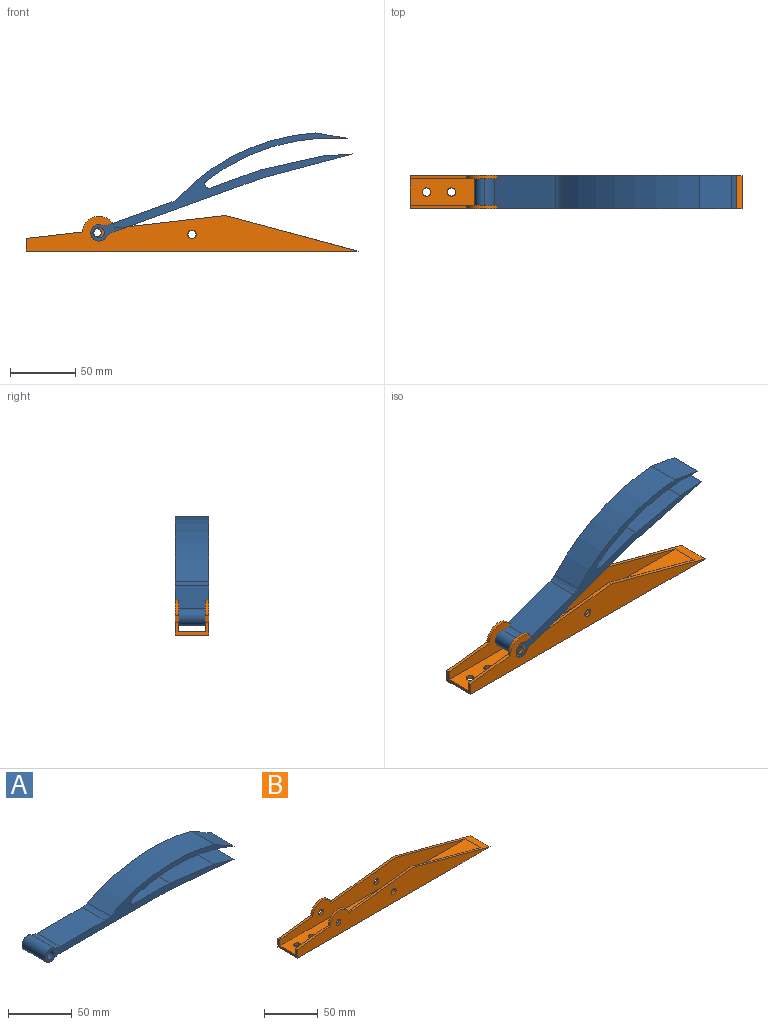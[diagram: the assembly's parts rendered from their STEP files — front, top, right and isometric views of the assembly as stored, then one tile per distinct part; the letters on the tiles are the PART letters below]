
ASSEMBLY  parts=2 mates=1
PART A: 17 faces, bbox 209.6x25.4x31.2 mm
  f0: plane 48.61x25.4mm, normal (0.13,0,0.99), area 1245.1mm2, adj f1,f9,f11,f12
  f1: plane 40.6x25.4mm, normal (0,0,1), area 1031.2mm2, adj f0,f11,f12,f16
  f2: cylinder r=157.48mm len=112.42mm, axis (0,-1,0), area 2924.4mm2, adj f3,f11,f12,f16
  f3: plane 25.4x21.43mm, normal (0.49,0,0.87), area 626mm2, adj f2,f4,f11,f12
  f4: cylinder r=157.48mm len=115.62mm, axis (0,-1,0), area 3020.8mm2, adj f3,f11,f12,f13
  f5: plane 49.86x25.4mm, normal (0,0,1), area 1266.5mm2, adj f11,f12,f13,f14
  f6: cylinder r=6.35mm len=25.4mm, axis (0,-1,0), area 695.6mm2, adj f11,f12,f14,f15
  f7: plane 121.82x25.4mm, normal (0,0,-1), area 3094.3mm2, adj f8,f11,f12,f15
  f8: plane 70.85x25.4mm, normal (-0.09,0,-1), area 1806.7mm2, adj f7,f9,f11,f12
  f9: plane 25.4x22.24mm, normal (0.27,0,0.96), area 587.5mm2, adj f0,f8,f11,f12
  f10: cylinder r=3.94mm len=25.4mm, axis (0,-1,0), area 628.3mm2, adj f11,f12
  f11: plane 209.55x31.21mm, normal (0,1,0), area 1830.8mm2, adj f0,f1,f2,f3,f4,f5,f6,f7
  f12: plane 209.55x31.21mm, normal (0,-1,0), area 1830.8mm2, adj f0,f1,f2,f3,f4,f5,f6,f7
  f13: cylinder r=12.7mm len=25.4mm, axis (0,-1,0), area 151.8mm2, adj f4,f5,f11,f12
  f14: cylinder r=12.7mm len=25.4mm, axis (0,-1,0), area 188.9mm2, adj f5,f6,f11,f12
  f15: cylinder r=12.7mm len=25.4mm, axis (0,-1,0), area 188.9mm2, adj f6,f7,f11,f12
  f16: cylinder r=3.17mm len=25.4mm, axis (0,-1,0), area 228.3mm2, adj f1,f2,f11,f12
PART B: 20 faces, bbox 254x25.4x27.2 mm
  f0: plane 43.2x4.98mm, normal (-0.11,0,0.99), area 110.4mm2, adj f1,f4,f10,f13
  f1: cylinder r=12.7mm len=24.88mm, axis (0,-1,0), area 90.6mm2, adj f0,f2,f10,f13
  f2: plane 84.32x9.72mm, normal (-0.11,0,0.99), area 215.6mm2, adj f1,f3,f10,f13
  f3: plane 101.6x27.22mm, normal (0.26,0,0.97), area 733.8mm2, adj f2,f5,f6,f9,f10,f11,f12,f13
  f4: plane 25.4x9.65mm, normal (-1,0,0), area 100.6mm2, adj f0,f5,f8,f9,f10,f11,f12,f13
  f5: plane 254x25.4mm, normal (0,0,-1), area 6388.3mm2, adj f3,f4,f9,f10,f16,f17
  f6: plane 84.32x9.72mm, normal (-0.11,0,0.99), area 215.6mm2, adj f3,f7,f9,f12
  f7: cylinder r=12.7mm len=24.88mm, axis (0,-1,0), area 90.6mm2, adj f6,f8,f9,f12
  f8: plane 43.2x4.98mm, normal (-0.11,0,0.99), area 110.4mm2, adj f4,f7,f9,f12
  f9: plane 254x27.22mm, normal (0,1,0), area 4329.5mm2, adj f3,f4,f5,f6,f7,f8,f15,f19
  f10: plane 254x27.22mm, normal (0,-1,0), area 4329.5mm2, adj f0,f1,f2,f3,f4,f5,f14,f18
  f11: plane 244.52x20.32mm, normal (0,0,1), area 4905.3mm2, adj f3,f4,f12,f13,f16,f17
  f12: plane 244.52x24.68mm, normal (0,-1,0), area 3696.4mm2, adj f3,f4,f6,f7,f8,f11,f15,f19
  f13: plane 244.52x24.68mm, normal (0,1,0), area 3696.4mm2, adj f0,f1,f2,f3,f4,f11,f14,f18
  f14: cylinder r=3.17mm len=6.35mm, axis (0,-1,0), area 50.7mm2, adj f10,f13
  f15: cylinder r=3.17mm len=6.35mm, axis (0,-1,0), area 50.7mm2, adj f9,f12
  f16: cylinder r=3.17mm len=6.35mm, axis (0,0,1), area 50.7mm2, adj f5,f11
  f17: cylinder r=3.17mm len=6.35mm, axis (0,0,1), area 50.7mm2, adj f5,f11
  f18: cylinder r=3.17mm len=6.35mm, axis (0,-1,0), area 50.7mm2, adj f10,f13
  f19: cylinder r=3.17mm len=6.35mm, axis (0,-1,0), area 50.7mm2, adj f9,f12
PLACE A rot(axis=(0,-1,0),19.9deg) t=(4.5,28.42,-60.45)mm
PLACE B t=(27.77,28.42,-71.43)mm
MATE revolute B.f1 <-> A.f10  axis (0,-1,0) through (3.41,28.42,-57.46)mm
